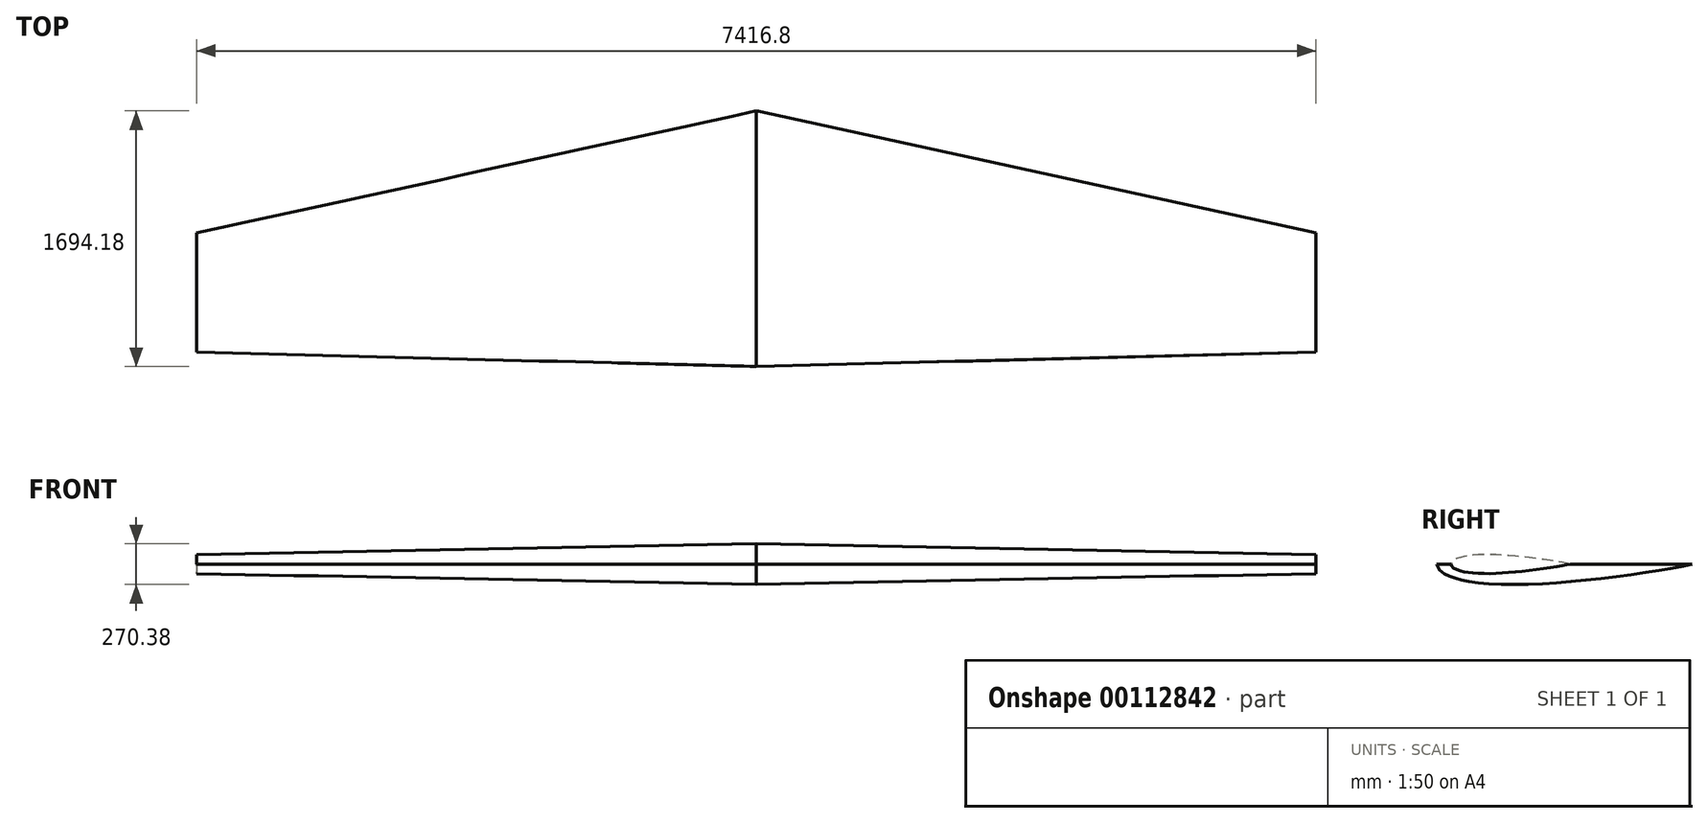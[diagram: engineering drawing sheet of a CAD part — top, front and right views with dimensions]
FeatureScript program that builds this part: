
annotation { "Feature Type Name" : "Feature", "Feature Type Description" : "" }
export const myFeature = defineFeature(function(context is Context, id is Id, definition is map)
    precondition{}
    {
        {
            var Q0;
            Q0=qCreatedBy(makeId("Right.planeOp"),FACE);
            var sketch = newSketch(context, id + "F0", { "sketchPlane" : qUnion([Q0])});
            skPoint(sketch, "E0", {"position": v(-794.31, -0.2) * mm});
            skLineSegment(sketch, "E1", {"start": v(-794.31, -0.2) * mm, "end": v(899.87, -0.2) * mm, "construction": true});
            skSolve(sketch);
        }
        {
            var Q0;
            Q0=qCreatedBy(makeId("Right.planeOp"),FACE);
            cPlane(context, id + "F1", {"entities" : qUnion([Q0]), "cplaneType" : CPlaneType.OFFSET, "offset" : 3708.4 * mm, "width" : 152.4 * mm, "height" : 152.4 * mm});
        }
        {
            var Q0;
            Q0=qCreatedBy(makeId("Right.planeOp"),FACE);
            var sketch = newSketch(context, id + "F2", { "sketchPlane" : qUnion([Q0])});
            skPoint(sketch, "E2.0", {"position": v(-794.31, -0.2) * mm});
            skFitSpline(sketch, "E3", {"points": [v(-794.31, -0.2) * mm, v(-763.75, 49.97) * mm, v(-722.84, 73.15) * mm, v(-679.5, 90.38) * mm, v(-627.74, 104.39) * mm, v(-536.62, 120.74) * mm, v(-358.55, 133.75) * mm, v(-102.86, 130.66) * mm, v(179.46, 107.57) * mm, v(493.76, 69.46) * mm, v(737.34, 32.27) * mm, v(899.87, -0.2) * mm], "startDerivative": vector(5.33, 1023.15) * mm, "endDerivative": vector(1915.45, -476.94) * mm});
            skLineSegment(sketch, "E4.0", {"start": v(-794.31, -0.2) * mm, "end": v(899.87, -0.2) * mm, "construction": true});
            skFitSpline(sketch, "E5.MirrorCS", {"points": [v(-794.31, -0.2) * mm, v(-763.75, -50.4) * mm, v(-722.84, -73.56) * mm, v(-679.5, -90.8) * mm, v(-627.74, -104.8) * mm, v(-536.62, -121.16) * mm, v(-358.55, -134.17) * mm, v(-102.86, -131.08) * mm, v(179.46, -107.99) * mm, v(493.76, -69.88) * mm, v(737.34, -32.69) * mm, v(899.87, -0.2) * mm], "startDerivative": vector(5.33, -1023.15) * mm, "endDerivative": vector(1915.45, 476.94) * mm});
            skSolve(sketch);
        }
        {
            var Q0;
            Q0=qCreatedBy(makeId("Top.planeOp"),FACE);
            var sketch = newSketch(context, id + "F3", { "sketchPlane" : qUnion([Q0])});
            skPoint(sketch, "E6.0", {"position": v(0, -794.31) * mm});
            skPoint(sketch, "E7.0", {"position": v(0, 899.87) * mm});
            skLineSegment(sketch, "E8", {"start": v(0, 899.87) * mm, "end": v(0, -794.31) * mm});
            skLineSegment(sketch, "E9", {"start": v(0, -794.31) * mm, "end": v(3711.83, -699.47) * mm});
            skLineSegment(sketch, "E10", {"start": v(3711.83, -699.47) * mm, "end": v(3711.83, 90.83) * mm});
            skLineSegment(sketch, "E11", {"start": v(3711.83, 90.83) * mm, "end": v(0, 899.87) * mm});
            skSolve(sketch);
        }
        {
            var Q0;
            Q0=qCreatedBy(id+"F1.planeOp",FACE);
            var sketch = newSketch(context, id + "F4", { "sketchPlane" : qUnion([Q0])});
            skPoint(sketch, "E12", {"position": v(-699.47, 0) * mm});
            skLineSegment(sketch, "E13", {"start": v(-699.47, 0) * mm, "end": v(90.47, 0) * mm, "construction": true});
            skPoint(sketch, "E14.0", {"position": v(90.83, 0) * mm});
            skFitSpline(sketch, "E15", {"points": [v(-699.47, 0) * mm, v(-697.5, 9.93) * mm, v(-675.98, 29.24) * mm, v(-633.09, 45.7) * mm, v(-581.33, 55.83) * mm, v(-495.87, 62.48) * mm, v(-378.91, 60.9) * mm, v(-245.32, 49.6) * mm, v(-83.09, 29.87) * mm, v(43.05, 9.95) * mm, v(90.83, 0) * mm], "startDerivative": vector(-15.28, 180.49) * mm, "endDerivative": vector(515.25, -115.07) * mm});
            skFitSpline(sketch, "E16.MirrorCS", {"points": [v(-699.47, 0) * mm, v(-697.5, -9.93) * mm, v(-675.98, -29.24) * mm, v(-633.09, -45.7) * mm, v(-581.33, -55.83) * mm, v(-495.87, -62.48) * mm, v(-378.91, -60.9) * mm, v(-245.32, -49.6) * mm, v(-83.09, -29.87) * mm, v(43.05, -9.95) * mm, v(90.83, 0) * mm], "startDerivative": vector(-15.28, -180.49) * mm, "endDerivative": vector(515.25, 115.07) * mm});
            skSolve(sketch);
        }
        {
            var Q0;
            Q0=qSketchRegion(id+"F2",true);
            var Q1;
            Q1=qSketchRegion(id+"F4",true);
            loft(context, id + "F5", {"sheetProfilesArray" : [{ "sheetProfileEntities" : qUnion([Q0]) }, { "sheetProfileEntities" : qUnion([Q1]) }]});
        }
        {
            var Q0;
            Q0=makeQuery(id+"F5.opLoft","SWEPT_BODY",BODY,{"disambiguationData":[OSD([makeQuery(id+"F2.imprint","IMPRINT",FACE,{"disambiguationData":[TD([[makeQuery(id+"F2.imprint","IMPRINT",EDGE,{"derivedFrom":sQuery(id+"F2.wireOp",EDGE,"E3")}),-1.0]])]}),makeQuery(id+"F4.imprint","IMPRINT",FACE,{"disambiguationData":[TD([[makeQuery(id+"F4.imprint","IMPRINT",EDGE,{"derivedFrom":sQuery(id+"F4.wireOp",EDGE,"3cd4921b-702b-40df-833c-018ac261c9d4")}),-1.0]])]})])]});
            var Q1;
            Q1=qCreatedBy(makeId("Right.planeOp"),FACE);
            mirror(context, id + "F6", {"operationType" : NewBodyOperationType.ADD, "entities" : qUnion([Q0]), "mirrorPlane" : qUnion([Q1])});
        }
    });
